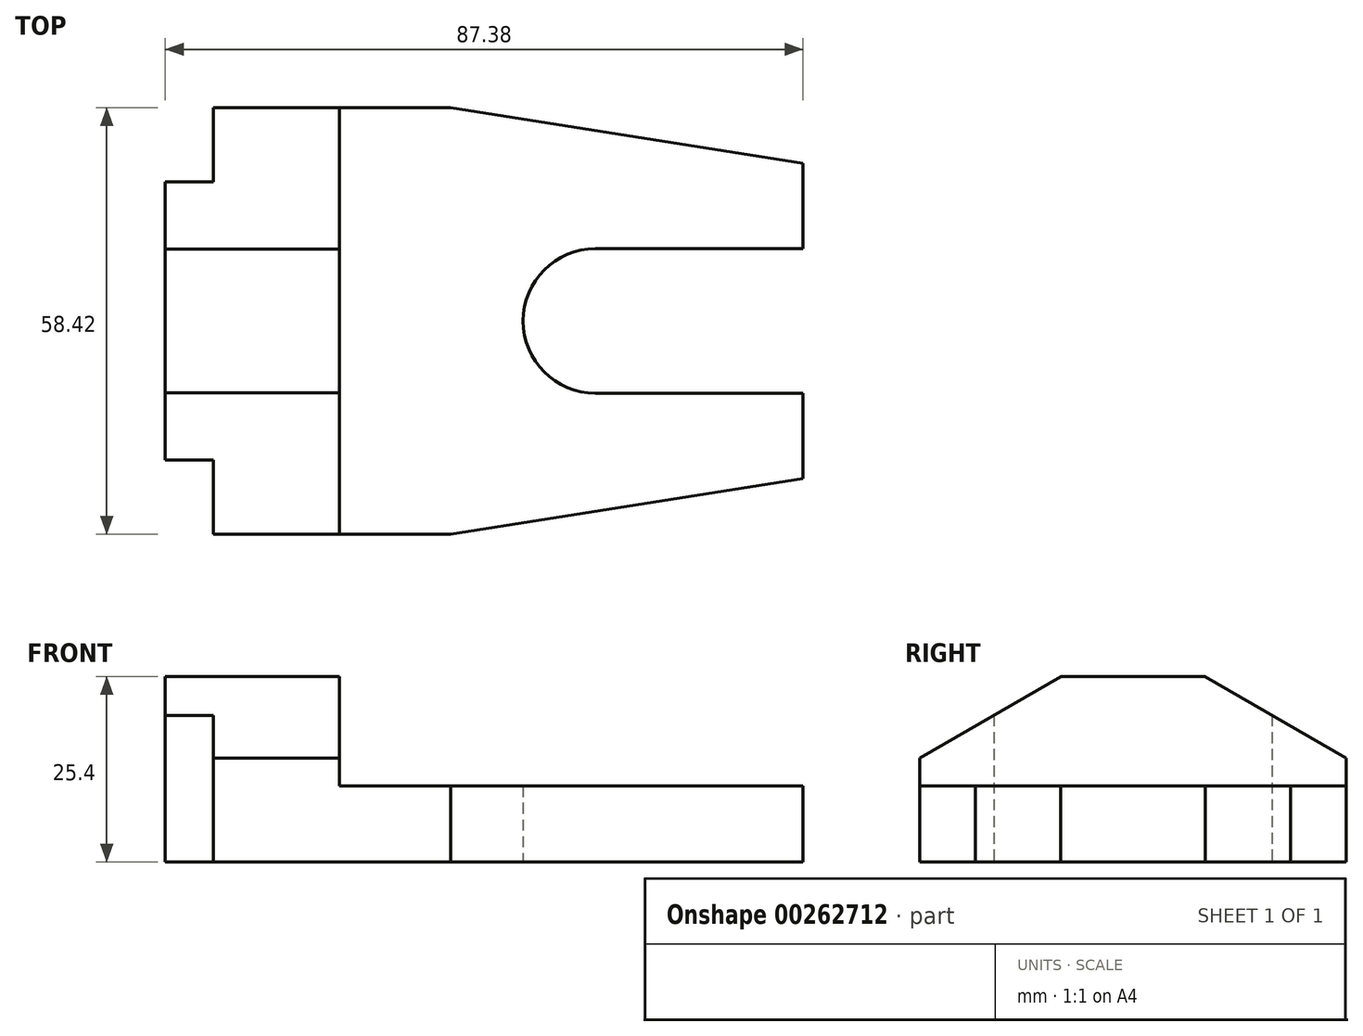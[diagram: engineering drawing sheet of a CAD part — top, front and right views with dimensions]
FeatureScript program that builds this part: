
annotation { "Feature Type Name" : "Feature", "Feature Type Description" : "" }
export const myFeature = defineFeature(function(context is Context, id is Id, definition is map)
    precondition{}
    {
        {
            var Q0;
            Q0=qCreatedBy(makeId("Top.planeOp"),FACE);
            var sketch = newSketch(context, id + "F0", { "sketchPlane" : qUnion([Q0])});
            skLineSegment(sketch, "E0.bottom", {"start": v(-30.87, 29.2) * mm, "end": v(1.64, 29.2) * mm});
            skLineSegment(sketch, "E0.top", {"start": v(-30.87, -29.21) * mm, "end": v(1.64, -29.21) * mm});
            skLineSegment(sketch, "E0.left", {"start": v(-37.48, 19.05) * mm, "end": v(-37.48, -19.05) * mm});
            skLineSegment(sketch, "E0.right", {"start": v(49.9, 21.59) * mm, "end": v(49.9, 9.9) * mm});
            skPoint(sketch, "E0.middle", {"position": v(0, 0) * mm});
            skLineSegment(sketch, "E1", {"start": v(49.9, 21.59) * mm, "end": v(1.64, 29.2) * mm});
            skLineSegment(sketch, "E2", {"start": v(1.64, -29.21) * mm, "end": v(49.9, -21.59) * mm});
            skLineSegment(sketch, "E3", {"start": v(-30.87, 29.2) * mm, "end": v(-30.87, 19.05) * mm});
            skLineSegment(sketch, "E4", {"start": v(-30.87, 19.05) * mm, "end": v(-37.48, 19.05) * mm});
            skLineSegment(sketch, "E5", {"start": v(-30.87, -29.21) * mm, "end": v(-30.87, -19.05) * mm});
            skLineSegment(sketch, "E6", {"start": v(-30.87, -19.05) * mm, "end": v(-37.48, -19.05) * mm});
            skArc(sketch, "E7", {"start": v(21.45, 9.9) * mm, "mid": v(11.55, 0) * mm, "end": v(21.45, -9.9) * mm});
            skLineSegment(sketch, "E8", {"start": v(21.45, 9.9) * mm, "end": v(49.9, 9.9) * mm});
            skLineSegment(sketch, "E9", {"start": v(21.45, -9.9) * mm, "end": v(49.9, -9.9) * mm});
            skLineSegment(sketch, "E10.trimOffspring", {"start": v(49.9, -9.9) * mm, "end": v(49.9, -21.59) * mm});
            skSolve(sketch);
        }
        {
            var Q0;
            Q0=makeQuery(id+"F0.imprint","IMPRINT",FACE,{"disambiguationData":[TD([[makeQuery(id+"F0.imprint","IMPRINT",EDGE,{"derivedFrom":sQuery(id+"F0.wireOp",EDGE,"E0.bottom")}),-1.0]])]});
            extrude(context, id + "F1", {"entities" : qUnion([Q0]), "depth" : 25.4 * mm});
        }
        {
            var Q0;
            Q0=makeQuery(id+"F1.opExtrude","SWEPT_FACE",FACE,{"disambiguationData":[OSD([sQuery(id+"F0.wireOp",EDGE,"E0.top")])]});
            var sketch = newSketch(context, id + "F2", { "sketchPlane" : qUnion([Q0])});
            skLineSegment(sketch, "E11", {"start": v(-13.6, 25.4) * mm, "end": v(-13.6, 10.41) * mm});
            skLineSegment(sketch, "E12", {"start": v(-13.6, 10.41) * mm, "end": v(50.39, 10.41) * mm});
            skLineSegment(sketch, "E13", {"start": v(50.39, 10.41) * mm, "end": v(50.39, 25.4) * mm});
            skLineSegment(sketch, "E14", {"start": v(50.39, 25.4) * mm, "end": v(-13.6, 25.4) * mm});
            skSolve(sketch);
        }
        {
            var Q0;
            {var subQ0=sQuery(id+"F2.wireOp",EDGE,"E11");Q0=makeQuery(id+"F2.imprint","IMPRINT",FACE,{"disambiguationData":[TD([[makeQuery(id+"F2.imprint","IMPRINT",EDGE,{"derivedFrom":subQ0}),1.0]])]});}
            var Q1;
            {var subQ0=sQuery(id+"F2.wireOp",EDGE,"E13");Q1=makeQuery(id+"F2.imprint","IMPRINT",FACE,{"disambiguationData":[TD([[makeQuery(id+"F2.imprint","IMPRINT",EDGE,{"derivedFrom":subQ0}),1.0]])]});}
            extrude(context, id + "F3", {"entities" : qUnion([Q0, Q1]), "operationType" : NewBodyOperationType.REMOVE, "oppositeDirection" : true, "depth" : 76.2 * mm});
        }
        {
            var Q0;
            Q0=makeQuery(id+"F3.boolean.opBoolean","COPY",FACE,{"derivedFrom":makeQuery(id+"F3.opExtrude","SWEPT_FACE",FACE,{"disambiguationData":[OSD([sQuery(id+"F2.wireOp",EDGE,"E11")])]})});
            var sketch = newSketch(context, id + "F4", { "sketchPlane" : qUnion([Q0])});
            skLineSegment(sketch, "E15", {"start": v(-9.85, 25.4) * mm, "end": v(-29.21, 14.22) * mm});
            skLineSegment(sketch, "E16", {"start": v(9.85, 25.4) * mm, "end": v(29.2, 14.22) * mm});
            skSolve(sketch);
        }
        {
            var Q0;
            {var subQ0=sQuery(id+"F4.wireOp",EDGE,"E15");Q0=makeQuery(id+"F4.imprint","IMPRINT",FACE,{"disambiguationData":[TD([[makeQuery(id+"F4.imprint","IMPRINT",EDGE,{"derivedFrom":subQ0}),-1.0]])]});}
            var Q1;
            {var subQ0=sQuery(id+"F4.wireOp",EDGE,"E16");Q1=makeQuery(id+"F4.imprint","IMPRINT",FACE,{"disambiguationData":[TD([[makeQuery(id+"F4.imprint","IMPRINT",EDGE,{"derivedFrom":subQ0}),1.0]])]});}
            extrude(context, id + "F5", {"entities" : qUnion([Q0, Q1]), "operationType" : NewBodyOperationType.REMOVE, "oppositeDirection" : true, "depth" : 25.4 * mm});
        }
    });
